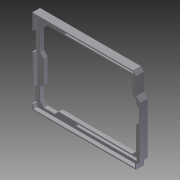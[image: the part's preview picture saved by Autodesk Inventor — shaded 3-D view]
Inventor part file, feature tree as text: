
AUTODESK INVENTOR PART (.ipt)
format: ipt  version: 2012 SP1 (Build 160190100, 190)  size: 262,656 bytes
history: native  units: in
note: dims shown in document units (in); Inventor stores cm internally (conversion verified against a paired STEP export)
features: extrude x5, sketch x5, chamfer x2, projected_geometry x1
ambient origin geometry x8: Origin, YZ Plane, XZ Plane, XY Plane, X Axis, Y Axis, Z Axis, Center Point
feature tree (13):
  extrude  "Extrusion2"  Depth=2.1in
  extrude  "Extrusion3"  Depth=2.04in
  extrude  "Extrusion4"  Depth=1.59in
  extrude  "Extrusion5"  Depth=2.6in
  extrude  "Extrusion7"  Depth=0.2in
  chamfer  "Chamfer3"  Distance=0.008in
  chamfer  "Chamfer5"  Distance=0.1in
  sketch  "Sketch1"  dims[d0=2.54in d1=2.1in]
  sketch  "Sketch2"  dims[d4=2.6in d5=2.04in]
  sketch  "Sketch4"  dims[d6=2.7in d7=1.59in]
  sketch  "Sketch5"  dims[d8=1.49in d9=2.6in]
  projected_geometry  "Projected Loop1"
  sketch  "Sketch7"  dims[d10=0.1in d11=0.2in d15=0.008in d16=0.1in d17=0.0in d18=0.029in d19=2.54in d20=2.1in d21=2.6in d22=2.04in d23=2.7in d24=1.59in d25=1.49in d26=2.6in d27=0.1in d28=0.2in d29=0.008in d30=0.029in d31=0.2in d32=0.1in d33=0.0in d35=0.49in d36=0.1125in d37=1.26in d38=1.74in d39=0.09in d40=0.0in d41=0.0625in d42=1.0in d43=2.55in d44=0.7in d45=2.55in d46=0.0625in d47=2.0312in d48=0.0688in d49=0.085in d50=0.0in d51=0.0in d52=0.475in d54=0.45in d56=1.198in d57=2.505in d58=0.2in d61=0.1in d66=0.1in d67=0.1in d68=0.1in d69=0.1in d70=0.55in d71=0.1in d72=0.125in d73=2.0in d74=0.125in d75=0.6in d76=2.6in d77=1.4in d78=0.125in d79=0.125in d80=2.6in d81=0.3in d97=0.1in d101=0.1in d102=0.1in d106=0.0625in d107=1.0in d108=2.55in d109=0.7in d110=2.55in d111=0.0625in d112=2.0312in d113=0.0688in d114=0.0in d115=0.475in d116=0.45in d117=0.1in d118=0.1in d119=0.1in d120=0.1in d121=0.1in d122=0.1in d123=0.1in d124=1.0in d125=0.0in d126=0.1in d127=0.125in d128=45.0deg d132=0.1in d133=0.125in d134=45.0deg]
